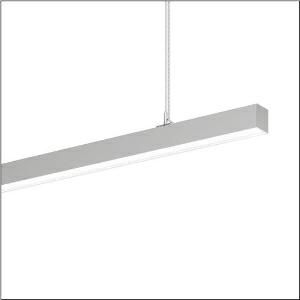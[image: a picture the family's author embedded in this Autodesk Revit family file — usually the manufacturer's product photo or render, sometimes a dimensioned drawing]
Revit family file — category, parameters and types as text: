
# Revit family: silica_r__21_51mx33da47sb_3209
name_source: partatom
category: Lighting Fixtures
units: mm (PartAtom-declared; Revit-internal decimal feet)

## family parameters
Cut with Voids When Loaded = No
Host = Face
Light Source = No
Part Type = Normal
Room Calculation Point = No
Round Connector Dimension = Use Diameter
Shared = No

## types (1)
- --- (1 x LED, 5910 lm, 38.4 W, 4000K)
    Apparent Load = 38 VA
    CIE Flux Codes = 78 96 99 55 100
    Color Rendering = 80
    Color Temperature = 4000K
    Default Elevation = 1800 mm
    Description = Silica® 21, office luminaire, primary optical cover: prismatic diffuser, of PMMA, CAT 2 (L<= 3000cd/m²), light emission: direct/indirect distribution, primary light characteristic: symmetric, installation type: suspended mounting, LED, rated luminous flux: 5.910lm, luminous efficacy: 154lm/W, light colour: 840, colour temperature: 4000K, with terminal, 3+2-pole, max. 2.5mm², mains connection: 220..240V, AC, 50/60Hz, rated input power: 38.4W, luminaire housing, of aluminium, metallic grey (RAL 9006), length: 1.204mm, width: 53mm, height: 53mm, protection rating (complete): IP20, insulation class (complete): insulation class I (protective earthing), certification: CE, permissible operating ambient temperature: 0..+35°C, standard: EN 50419, packaging unit: 1 piece
    Height = 53 mm
    Lamp = 1 x LED
    Lamp Light Flux = 5910 lm
    Lamp Power = 38.4 W
    Lamp count = 1
    Length = 1204 mm
    Luminous efficacy = 154 lm/W
    Manufacturer = Siteco
    ModVariant = No
    Model = 51MX33DA47SB
    Mounting Place = Ceiling
    Mounting Type = Pendant
    Number of Poles = 1
    OnlyDefault = Yes
    Power Factor = 1
    Product Name = Silica® 21
    Product group = office luminaire | ceiling pendant
    ProductGroupID = 902
    Protection Class = Protection class I
    Protection Degree = IP 20
    RLX_Detail_Level = 1
    RLX_Emergency_Light_Flux = 0 lm
    RLX_Emergency_Type = 0
    RLX_Emergency_Type_DB = No
    RlxData = <blob elided: 23133 chars, md5=6e216051>
    Socket = socket
    Standby Power = 0 W
    System Light Flux = 5910 lm
    System Power = 38 W
    Type Comments = factory setting: luminous flux: 100 % | dim-lin: 254 | 323 mA
    Type Image = l_1297747.jpg
    URL = http://relux.com
    VarID = @adj_048947
    Voltage = 0 V
    Weight = 0.00 kg
    Width = 53 mm

## geometry (parser evidence)
native form markers: Blend x4, Sweep x12
no freeform markers — native parametric forms only
